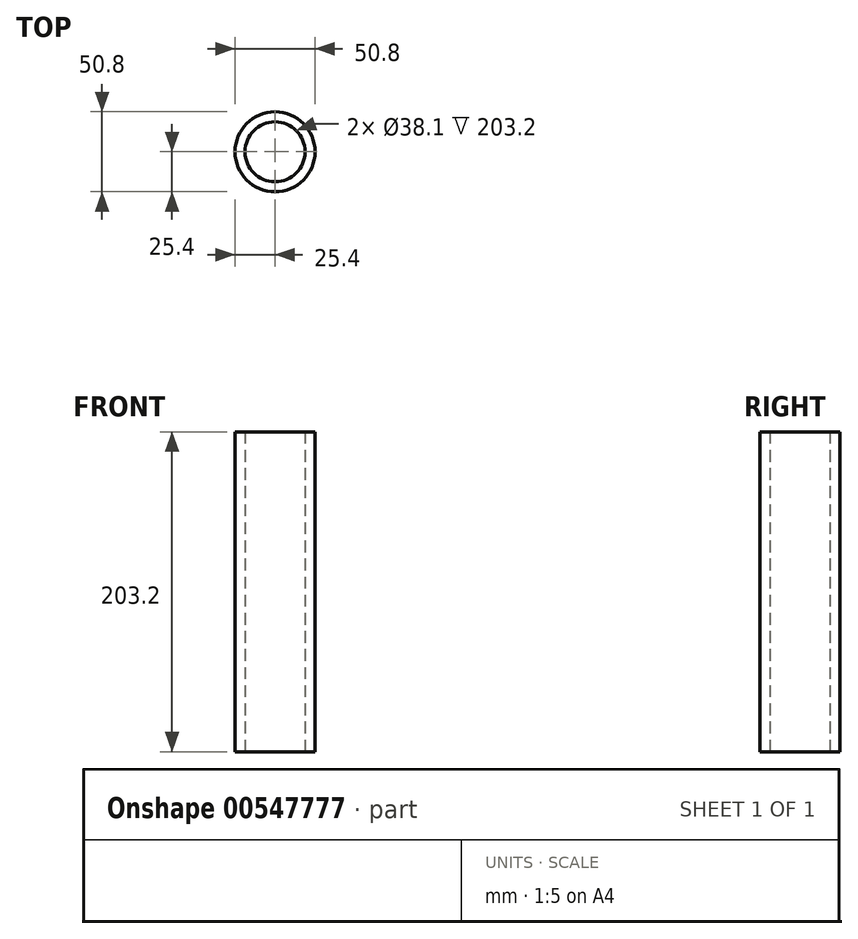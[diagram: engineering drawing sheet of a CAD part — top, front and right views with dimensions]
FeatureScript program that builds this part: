
annotation { "Feature Type Name" : "Feature", "Feature Type Description" : "" }
export const myFeature = defineFeature(function(context is Context, id is Id, definition is map)
    precondition{}
    {
        {
            var Q0;
            Q0=qCreatedBy(makeId("Top.planeOp"),FACE);
            var sketch = newSketch(context, id + "F0", { "sketchPlane" : qUnion([Q0])});
            skCircle(sketch, "E0", {"center": v(0, 0) * mm, "radius": 25.4 * mm});
            skSolve(sketch);
        }
        {
            var Q0;
            Q0=makeQuery(id+"F0.imprint","IMPRINT",FACE,{"disambiguationData":[TD([[makeQuery(id+"F0.imprint","IMPRINT",EDGE,{"derivedFrom":sQuery(id+"F0.wireOp",EDGE,"E0")}),1.0]])]});
            extrude(context, id + "F1", {"entities" : qUnion([Q0]), "endBound" : BoundingType.SYMMETRIC, "depth" : 203.2 * mm, "offsetDistance" : 25.4 * mm});
        }
        {
            var Q0;
            Q0=makeQuery(id+"F1.opExtrude","CAP_FACE",FACE,{"disambiguationData":[OSD([sQuery(id+"F0.wireOp",EDGE,"E0")])],"isStart":false});
            var Q1;
            Q1=makeQuery(id+"F1.opExtrude","CAP_FACE",FACE,{"disambiguationData":[OSD([sQuery(id+"F0.wireOp",EDGE,"E0")])],"isStart":true});
            shell(context, id + "F2", {"entities" : qUnion([Q0, Q1]), "thickness" : 6.35 * mm});
        }
    });
